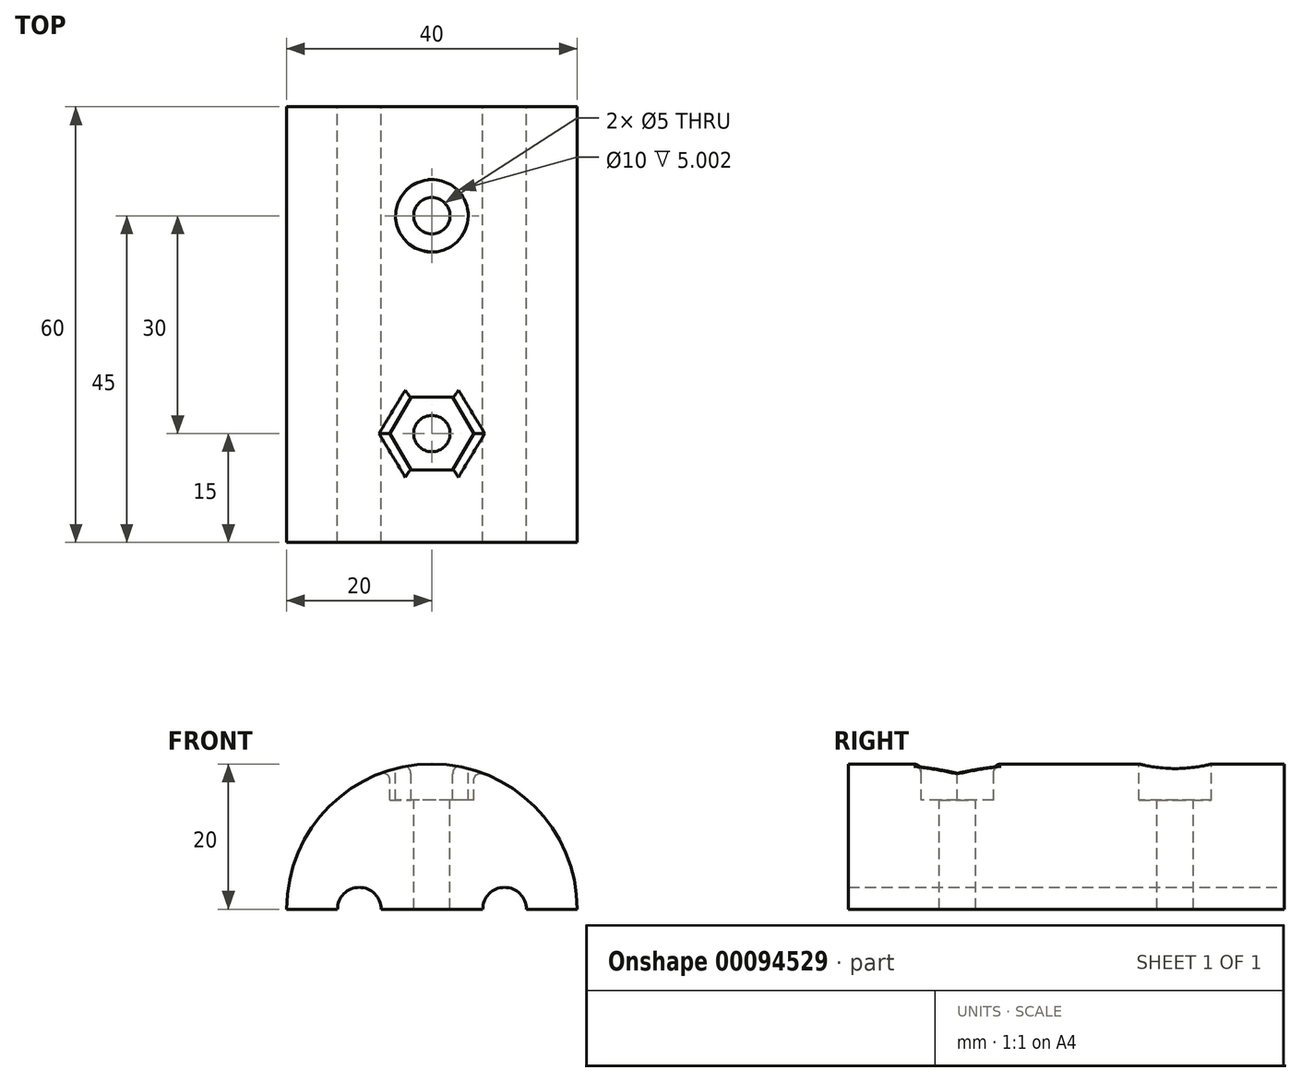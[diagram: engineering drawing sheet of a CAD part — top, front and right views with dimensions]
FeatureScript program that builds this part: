
annotation { "Feature Type Name" : "Feature", "Feature Type Description" : "" }
export const myFeature = defineFeature(function(context is Context, id is Id, definition is map)
    precondition{}
    {
        {
            var Q0;
            Q0=qCreatedBy(makeId("Front.planeOp"),FACE);
            var sketch = newSketch(context, id + "F0", { "sketchPlane" : qUnion([Q0])});
            skArc(sketch, "E0", {"start": v(20, 0) * mm, "mid": v(0, 20) * mm, "end": v(-20, 0) * mm});
            skLineSegment(sketch, "E1", {"start": v(-20, 0) * mm, "end": v(-10, 0) * mm});
            skArc(sketch, "E2", {"start": v(-7, 0) * mm, "mid": v(-10, 3) * mm, "end": v(-13, 0) * mm});
            skLineSegment(sketch, "E3.trimOffspring", {"start": v(-7, 0) * mm, "end": v(10, 0) * mm});
            skArc(sketch, "E4.MirrorCS", {"start": v(7, 0) * mm, "mid": v(10, 3) * mm, "end": v(13, 0) * mm});
            skLineSegment(sketch, "E5.trimOffspring", {"start": v(13, 0) * mm, "end": v(20, 0) * mm});
            skLineSegment(sketch, "E6", {"start": v(-44, 26.74) * mm, "end": v(-44, -17.93) * mm, "construction": true});
            skSolve(sketch);
        }
        {
            var Q0;
            Q0 = qSketchRegion(id + "F0", true);
            var Q1;
            {var subQ4=sQuery(id+"F0.wireOp",EDGE,"E0");Q1=makeQuery(id+"F0.imprint","IMPRINT",FACE,{"disambiguationData":[TD([[makeQuery(id+"F0.imprint","IMPRINT",EDGE,{"derivedFrom":subQ4}),1.0]])]});}
            extrude(context, id + "F1", {"entities" : qUnion([Q0, Q1]), "depth" : 60 * mm});
        }
        {
            var Q0;
            Q0=makeQuery(id+"F1.opExtrude","SWEPT_FACE",FACE,{"disambiguationData":[OSD([sQuery(id+"F0.wireOp",EDGE,"E3.trimOffspring")])]});
            var sketch = newSketch(context, id + "F2", { "sketchPlane" : qUnion([Q0])});
            skCircle(sketch, "E7", {"center": v(0, 15) * mm, "radius": 5 * mm});
            skLineSegment(sketch, "E8", {"start": v(0, 60) * mm, "end": v(0, 0) * mm, "construction": true});
            skLineSegment(sketch, "E9", {"start": v(-20.26, 30) * mm, "end": v(19.97, 30) * mm, "construction": true});
            skPoint(sketch, "E9.startSnap0", {"position": v(-7, 30) * mm});
            skCircle(sketch, "E10.MirrorC", {"center": v(0, 45) * mm, "radius": 5 * mm});
            skSolve(sketch);
        }
        {
            var Q0;
            Q0 = qSketchRegion(id + "F2", true);
            extrude(context, id + "F3", {"entities" : qUnion([Q0]), "operationType" : NewBodyOperationType.ADD, "oppositeDirection" : true, "depth" : 20 * mm});
        }
        {
            var Q0;
            Q0=makeQuery(id+"F3.opExtrude","CAP_FACE",FACE,{"disambiguationData":[OSD([sQuery(id+"F2.wireOp",EDGE,"E10.MirrorC")])],"isStart":false});
            var sketch = newSketch(context, id + "F4", { "sketchPlane" : qUnion([Q0])});
            skCircle(sketch, "E11.cCircle", {"center": v(0, -45) * mm, "radius": 5 * mm, "construction": true});
            skLineSegment(sketch, "E11.0", {"start": v(-2.89, -40) * mm, "end": v(2.89, -40) * mm});
            skLineSegment(sketch, "E11.1", {"start": v(2.89, -40) * mm, "end": v(5.77, -45) * mm});
            skLineSegment(sketch, "E11.2", {"start": v(5.77, -45) * mm, "end": v(2.89, -50) * mm});
            skLineSegment(sketch, "E11.3", {"start": v(2.89, -50) * mm, "end": v(-2.89, -50) * mm});
            skLineSegment(sketch, "E11.4", {"start": v(-2.89, -50) * mm, "end": v(-5.77, -45) * mm});
            skLineSegment(sketch, "E11.5", {"start": v(-5.77, -45) * mm, "end": v(-2.89, -40) * mm});
            skPoint(sketch, "E11.0.midPoint", {"position": v(0, -40) * mm});
            skCircle(sketch, "E12", {"center": v(0, -45) * mm, "radius": 2.5 * mm});
            skLineSegment(sketch, "E13", {"start": v(0, -59.95) * mm, "end": v(0, 0) * mm, "construction": true});
            skCircle(sketch, "E14", {"center": v(0, -15) * mm, "radius": 2.5 * mm});
            skCircle(sketch, "E15", {"center": v(0, -15) * mm, "radius": 5 * mm});
            skSolve(sketch);
        }
        {
            var Q0;
            Q0=makeQuery(id+"F4.imprint","IMPRINT",FACE,{"disambiguationData":[TD([[makeQuery(id+"F4.imprint","IMPRINT",EDGE,{"derivedFrom":sQuery(id+"F4.wireOp",EDGE,"E12")}),-1.0]])]});
            var Q1;
            {var subQ0=sQuery(id+"F4.wireOp",EDGE,"E11.0");var subQ4=sQuery(id+"F4.wireOp",EDGE,"E11.1");var subQ5=makeQuery(id+"F4.imprint","INTERSECT",VERTEX,{"derivedFrom":[subQ0,subQ4]});Q1=makeQuery(id+"F4.imprint","IMPRINT",FACE,{"disambiguationData":[TD([[makeQuery(id+"F4.imprint","IMPRINT",EDGE,{"disambiguationData":[TD([[subQ5,-1.0]])],"derivedFrom":subQ4}),-1.0]])]});}
            var Q2;
            {var subQ0=sQuery(id+"F4.wireOp",EDGE,"E11.0");var subQ4=sQuery(id+"F4.wireOp",EDGE,"E11.5");var subQ5=makeQuery(id+"F4.imprint","INTERSECT",VERTEX,{"derivedFrom":[subQ0,subQ4]});Q2=makeQuery(id+"F4.imprint","IMPRINT",FACE,{"disambiguationData":[TD([[makeQuery(id+"F4.imprint","IMPRINT",EDGE,{"disambiguationData":[TD([[subQ5,1.0]])],"derivedFrom":subQ4}),-1.0]])]});}
            var Q3;
            {var subQ0=sQuery(id+"F4.wireOp",EDGE,"E11.2");var subQ1=sQuery(id+"F4.wireOp",EDGE,"E11.1");var subQ2=makeQuery(id+"F4.imprint","INTERSECT",VERTEX,{"derivedFrom":[subQ1,subQ0]});Q3=makeQuery(id+"F4.imprint","IMPRINT",FACE,{"disambiguationData":[TD([[makeQuery(id+"F4.imprint","IMPRINT",EDGE,{"disambiguationData":[TD([[subQ2,1.0]])],"derivedFrom":subQ1}),-1.0]])]});}
            var Q4;
            {var subQ0=sQuery(id+"F4.wireOp",EDGE,"E11.3");var subQ4=sQuery(id+"F4.wireOp",EDGE,"E11.4");var subQ5=makeQuery(id+"F4.imprint","INTERSECT",VERTEX,{"derivedFrom":[subQ0,subQ4]});Q4=makeQuery(id+"F4.imprint","IMPRINT",FACE,{"disambiguationData":[TD([[makeQuery(id+"F4.imprint","IMPRINT",EDGE,{"disambiguationData":[TD([[subQ5,-1.0]])],"derivedFrom":subQ4}),-1.0]])]});}
            var Q5;
            {var subQ0=sQuery(id+"F4.wireOp",EDGE,"E11.5");var subQ1=sQuery(id+"F4.wireOp",EDGE,"E11.4");var subQ2=makeQuery(id+"F4.imprint","INTERSECT",VERTEX,{"derivedFrom":[subQ1,subQ0]});Q5=makeQuery(id+"F4.imprint","IMPRINT",FACE,{"disambiguationData":[TD([[makeQuery(id+"F4.imprint","IMPRINT",EDGE,{"disambiguationData":[TD([[subQ2,1.0]])],"derivedFrom":subQ1}),-1.0]])]});}
            var Q6;
            {var subQ0=sQuery(id+"F4.wireOp",EDGE,"E11.3");var subQ1=sQuery(id+"F4.wireOp",EDGE,"E11.2");var subQ2=makeQuery(id+"F4.imprint","INTERSECT",VERTEX,{"derivedFrom":[subQ1,subQ0]});Q6=makeQuery(id+"F4.imprint","IMPRINT",FACE,{"disambiguationData":[TD([[makeQuery(id+"F4.imprint","IMPRINT",EDGE,{"disambiguationData":[TD([[subQ2,1.0]])],"derivedFrom":subQ1}),-1.0]])]});}
            var Q7;
            Q7=makeQuery(id+"F4.imprint","IMPRINT",FACE,{"disambiguationData":[TD([[makeQuery(id+"F4.imprint","IMPRINT",EDGE,{"derivedFrom":sQuery(id+"F4.wireOp",EDGE,"E14")}),-1.0]])]});
            extrude(context, id + "F5", {"entities" : qUnion([Q0, Q1, Q2, Q3, Q4, Q5, Q6, Q7]), "operationType" : NewBodyOperationType.REMOVE, "oppositeDirection" : true, "depth" : 5 * mm});
        }
        {
            var Q0;
            Q0=makeQuery(id+"F3.opExtrude","CAP_FACE",FACE,{"disambiguationData":[OSD([sQuery(id+"F2.wireOp",EDGE,"E10.MirrorC")])],"isStart":false});
            var Q1;
            Q1=makeQuery(id+"F3.opExtrude","CAP_FACE",FACE,{"disambiguationData":[OSD([sQuery(id+"F2.wireOp",EDGE,"E7")])],"isStart":false});
            extrude(context, id + "F6", {"entities" : qUnion([Q0, Q1]), "operationType" : NewBodyOperationType.REMOVE, "oppositeDirection" : true, "depth" : 20 * mm});
        }
        {
            var Q0;
            {var subQ0=makeQuery(id+"F3.opExtrude","SWEPT_FACE",FACE,{"disambiguationData":[OSD([sQuery(id+"F2.wireOp",EDGE,"E7")])]});var subQ1=makeQuery(id+"F1.opExtrude","SWEPT_FACE",FACE,{"disambiguationData":[OSD([sQuery(id+"F0.wireOp",EDGE,"E0")])]});Q0=makeQuery(id+"F5.boolean.opBoolean","MERGE",EDGE,{"derivedFrom":[makeQuery(id+"F3.boolean.opBoolean","INTERSECT",EDGE,{"disambiguationData":[OD(0.0)],"derivedFrom":[subQ1,subQ0]}),makeQuery(id+"F3.boolean.opBoolean","INTERSECT",EDGE,{"disambiguationData":[OD(1.0)],"derivedFrom":[subQ1,subQ0]})]});}
            var Q1;
            Q1=makeQuery(id+"F5.boolean.opBoolean","INTERSECT",EDGE,{"derivedFrom":[makeQuery(id+"F1.opExtrude","SWEPT_FACE",FACE,{"disambiguationData":[OSD([sQuery(id+"F0.wireOp",EDGE,"E0")])]}),makeQuery(id+"F5.opExtrude","SWEPT_FACE",FACE,{"disambiguationData":[OSD([sQuery(id+"F4.wireOp",EDGE,"E11.0")])]})]});
            var Q2;
            Q2=makeQuery(id+"F5.boolean.opBoolean","INTERSECT",EDGE,{"derivedFrom":[makeQuery(id+"F1.opExtrude","SWEPT_FACE",FACE,{"disambiguationData":[OSD([sQuery(id+"F0.wireOp",EDGE,"E0")])]}),makeQuery(id+"F5.opExtrude","SWEPT_FACE",FACE,{"disambiguationData":[OSD([sQuery(id+"F4.wireOp",EDGE,"E11.1")])]})]});
            var Q3;
            Q3=makeQuery(id+"F5.boolean.opBoolean","INTERSECT",EDGE,{"derivedFrom":[makeQuery(id+"F1.opExtrude","SWEPT_FACE",FACE,{"disambiguationData":[OSD([sQuery(id+"F0.wireOp",EDGE,"E0")])]}),makeQuery(id+"F5.opExtrude","SWEPT_FACE",FACE,{"disambiguationData":[OSD([sQuery(id+"F4.wireOp",EDGE,"E11.2")])]})]});
            var Q4;
            Q4=makeQuery(id+"F5.boolean.opBoolean","INTERSECT",EDGE,{"derivedFrom":[makeQuery(id+"F1.opExtrude","SWEPT_FACE",FACE,{"disambiguationData":[OSD([sQuery(id+"F0.wireOp",EDGE,"E0")])]}),makeQuery(id+"F5.opExtrude","SWEPT_FACE",FACE,{"disambiguationData":[OSD([sQuery(id+"F4.wireOp",EDGE,"E11.3")])]})]});
            var Q5;
            Q5=makeQuery(id+"F5.boolean.opBoolean","INTERSECT",EDGE,{"derivedFrom":[makeQuery(id+"F1.opExtrude","SWEPT_FACE",FACE,{"disambiguationData":[OSD([sQuery(id+"F0.wireOp",EDGE,"E0")])]}),makeQuery(id+"F5.opExtrude","SWEPT_FACE",FACE,{"disambiguationData":[OSD([sQuery(id+"F4.wireOp",EDGE,"E11.4")])]})]});
            var Q6;
            Q6=makeQuery(id+"F5.boolean.opBoolean","INTERSECT",EDGE,{"derivedFrom":[makeQuery(id+"F1.opExtrude","SWEPT_FACE",FACE,{"disambiguationData":[OSD([sQuery(id+"F0.wireOp",EDGE,"E0")])]}),makeQuery(id+"F5.opExtrude","SWEPT_FACE",FACE,{"disambiguationData":[OSD([sQuery(id+"F4.wireOp",EDGE,"E11.5")])]})]});
            fillet(context, id + "F7", {"entities" : qUnion([Q0, Q1, Q2, Q3, Q4, Q5, Q6]), "radius" : 1 * mm, "tangentPropagation" : true, "allowEdgeOverflow" : false});
        }
    });
